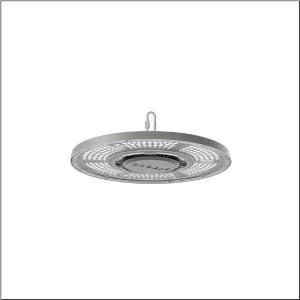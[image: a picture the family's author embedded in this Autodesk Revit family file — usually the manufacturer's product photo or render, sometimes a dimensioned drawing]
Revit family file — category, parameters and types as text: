
# Revit family: highbay_31-s_51hc427a4jmb
name_source: partatom
category: Lighting Fixtures
units: mm (PartAtom-declared; Revit-internal decimal feet)

## family parameters
Cut with Voids When Loaded = No
Host = Face
Light Source = No
Part Type = Normal
Room Calculation Point = No
Round Connector Dimension = Use Diameter
Shared = No

## types (1)
- Highbay 31-S (1 x LED, 20000 lm, 134 W, 4000K)
    Apparent Load = 134 VA
    CIE Flux Codes = 77 99 100 100 100
    Color Rendering = 80
    Color Temperature = 4000K
    Default Elevation = 1800 mm
    Description = Highbay 31-S, LED high bay luminaire, primary light control with lens, of PC, primary optical cover: cover panel, of PC, transparent, light emission: direct distribution, primary light characteristic: rotationally symmetric, installation type: suspended mounting, surface-mounted, LED, rated luminous flux: 20.000lm, luminous efficacy: 150lm/W, light colour: 840, colour temperature: 4000K, control gear: ECG, with cable, 3x 1.0mm², free wire ends, mains connection: 220..240V, AC/DC, 0/50..60Hz, cable length: 1,5m, rated input power: 134W, housing, rotationally symmetric, of diecast aluminium, powder-coated, grey aluminium (RAL 9007), with hook on luminaire side, incl. screw, diameter: 339mm, protection rating (complete): IP65, insulation class (complete): insulation class I (protective earthing), certification: CE, ENEC, UKCA, protection symbol: D, impact resistance: IK08, permissible operating ambient temperature: -30..+45°C, standard: EN 60598-2-22, EN 60598, corresponds to IFS (International Featured Standards) requirements for safety and quality in the food industry, packaging unit: 1 piece
    Height = 141 mm
    Lamp = 1 x LED
    Lamp Light Flux = 20000 lm
    Lamp Power = 134 W
    Lamp count = 1
    Length = 339 mm
    Luminous efficacy = 149 lm/W
    Manufacturer = Siteco
    ModVariant = No
    Model = 51HC427A4JMB
    Mounting Place = Ceiling
    Mounting Type = Pendant
    Number of Poles = 1
    OnlyDefault = Yes
    Power Factor = 1
    Product Name = Highbay 31-S
    Product group = LED high bay luminaire
    ProductGroupID = 903
    Protection Class = Protection class I
    Protection Degree = IP 65
    RLX_Detail_Level = 1
    RLX_Emergency_Light_Flux = 0 lm
    RLX_Emergency_Type = 0
    RLX_Emergency_Type_DB = No
    RlxData = <blob elided: 162797 chars, md5=30350c25>
    Socket = socket
    Standby Power = 0 W
    System Light Flux = 20000 lm
    System Power = 134 W
    Type Comments = Product without accessories
    Type Image = l_1007237.jpg
    URL = http://relux.com
    VarID = ---
    Voltage = 0 V
    Weight = 0.00 kg
    Width = 0 mm  [stored 0 ft]

note: [stored X ft] marks values corroborated as IEEE doubles in the binary element streams (Revit-internal decimal feet)

## geometry (parser evidence)
native form markers: Blend x4, Sweep x9
no freeform markers — native parametric forms only
